# Revit family: М_Eng
name_source: partatom
category: Mechanical Equipment
units: mm (PartAtom-declared; Revit-internal decimal feet)

## family parameters
Always vertical = Yes
Classification = None
Cut with Voids When Loaded = No
Part Type = Normal
Room Calculation Point = No
Round Connector Dimension = Use Diameter
Shared = No
Work Plane-Based = No

## types (9) — shared parameters
00_20_Manufacturer = Vents
00_20_Name = Axial fan
Casing Material = Plastic, opaque, white
Frequency = 50 Hz
Load Classification = HVAC
Maintenance zone material = <By Category>
Manufacturer = Vents
Number of Fase = 1
URL = https://ventilation-system.com
Voltage = 230 V
zero-valued in all types: Default Elevation

## per-type parameters (varying)
| type | 00_20_Type | Amperage | B | D | Diameter | Dy | H | Height | L | L1 | L2 | Length | Maximum Air Flow | Power | Sound pressure level at 3 m distance | Weight | Width |
| 150 M | 150 M | 0.130 A | 206 mm  [stored 0.675853 ft] | 150 mm | 150 mm | 145 mm  [stored 0.475722 ft] | 206 mm  [stored 0.675853 ft] | 206 mm  [stored 0.675853 ft] | 106 mm  [stored 0.347769 ft] | 26 mm | 81 mm | 106 mm  [stored 0.347769 ft] | 295.0 m³/h | 24 W | 39 dBA | 0.89 kg | 206 mm  [stored 0.675853 ft] |
| 100 М | 100 M | 0.090 A | 159 mm  [stored 0.521654 ft] | 100 mm  [stored 0.328084 ft] | 100 mm  [stored 0.328084 ft] | 95 mm  [stored 0.31168 ft] | 159 mm  [stored 0.521654 ft] | 159 mm  [stored 0.521654 ft] | 89 mm | 23 mm  [stored 0.0754593 ft] | 66 mm | 89 mm | 98.0 m³/h | 14 W | 34 dBA | 0.55 kg | 159 mm  [stored 0.521654 ft] |
| 125 М | 125 М | 0.100 A | 180 mm  [stored 0.590551 ft] | 125 mm  [stored 0.410105 ft] | 125 mm  [stored 0.410105 ft] | 120 mm  [stored 0.393701 ft] | 180 mm  [stored 0.590551 ft] | 180 mm  [stored 0.590551 ft] | 94 mm  [stored 0.308399 ft] | 25 mm  [stored 0.082021 ft] | 69 mm  [stored 0.226378 ft] | 94 mm  [stored 0.308399 ft] | 185.0 m³/h | 16 W | 35 dBA | 0.70 kg | 180 mm  [stored 0.590551 ft] |
| 100 М turbo | 100 М turbo | 0.100 A | 159 mm  [stored 0.521654 ft] | 100 mm  [stored 0.328084 ft] | 100 mm  [stored 0.328084 ft] | 95 mm  [stored 0.31168 ft] | 159 mm  [stored 0.521654 ft] | 159 mm  [stored 0.521654 ft] | 89 mm | 23 mm  [stored 0.0754593 ft] | 66 mm | 89 mm | 128.0 m³/h | 16 W | 37 dBA | 0.57 kg | 159 mm  [stored 0.521654 ft] |
| 100 М press | 100 М press | 0.100 A | 159 mm  [stored 0.521654 ft] | 100 mm  [stored 0.328084 ft] | 100 mm  [stored 0.328084 ft] | 95 mm  [stored 0.31168 ft] | 159 mm  [stored 0.521654 ft] | 159 mm  [stored 0.521654 ft] | 89 mm | 23 mm  [stored 0.0754593 ft] | 66 mm | 89 mm | 99.0 m³/h | 16 W | 37 dBA | 0.65 kg | 159 mm  [stored 0.521654 ft] |
| 125 М turbo | 125 М turbo | 0.105 A | 180 mm  [stored 0.590551 ft] | 125 mm  [stored 0.410105 ft] | 125 mm  [stored 0.410105 ft] | 120 mm  [stored 0.393701 ft] | 180 mm  [stored 0.590551 ft] | 180 mm  [stored 0.590551 ft] | 94 mm  [stored 0.308399 ft] | 25 mm  [stored 0.082021 ft] | 69 mm  [stored 0.226378 ft] | 94 mm  [stored 0.308399 ft] | 232.0 m³/h | 22 W | 37 dBA | 0.72 kg | 180 mm  [stored 0.590551 ft] |
| 125 М press | 125 М press | 0.105 A | 180 mm  [stored 0.590551 ft] | 125 mm  [stored 0.410105 ft] | 125 mm  [stored 0.410105 ft] | 120 mm  [stored 0.393701 ft] | 180 mm  [stored 0.590551 ft] | 180 mm  [stored 0.590551 ft] | 94 mm  [stored 0.308399 ft] | 25 mm  [stored 0.082021 ft] | 69 mm  [stored 0.226378 ft] | 94 mm  [stored 0.308399 ft] | 188.0 m³/h | 22 W | 39 dBA | 0.81 kg | 180 mm  [stored 0.590551 ft] |
| 150 М turbo | 150 М turbo | 0.130 A | 206 mm  [stored 0.675853 ft] | 150 mm | 150 mm | 145 mm  [stored 0.475722 ft] | 206 mm  [stored 0.675853 ft] | 206 mm  [stored 0.675853 ft] | 106 mm  [stored 0.347769 ft] | 26 mm | 81 mm | 106 mm  [stored 0.347769 ft] | 345.0 m³/h | 29 W | 41 dBA | 0.93 kg | 206 mm  [stored 0.675853 ft] |
| 150 М press | 150 М press | 0.130 A | 206 mm  [stored 0.675853 ft] | 150 mm | 150 mm | 145 mm  [stored 0.475722 ft] | 206 mm  [stored 0.675853 ft] | 206 mm  [stored 0.675853 ft] | 106 mm  [stored 0.347769 ft] | 26 mm | 81 mm | 106 mm  [stored 0.347769 ft] | 307.0 m³/h | 29 W | 41 dBA | 0.99 kg | 206 mm  [stored 0.675853 ft] |

note: [stored X ft] marks values corroborated as IEEE doubles in the binary element streams (Revit-internal decimal feet)
